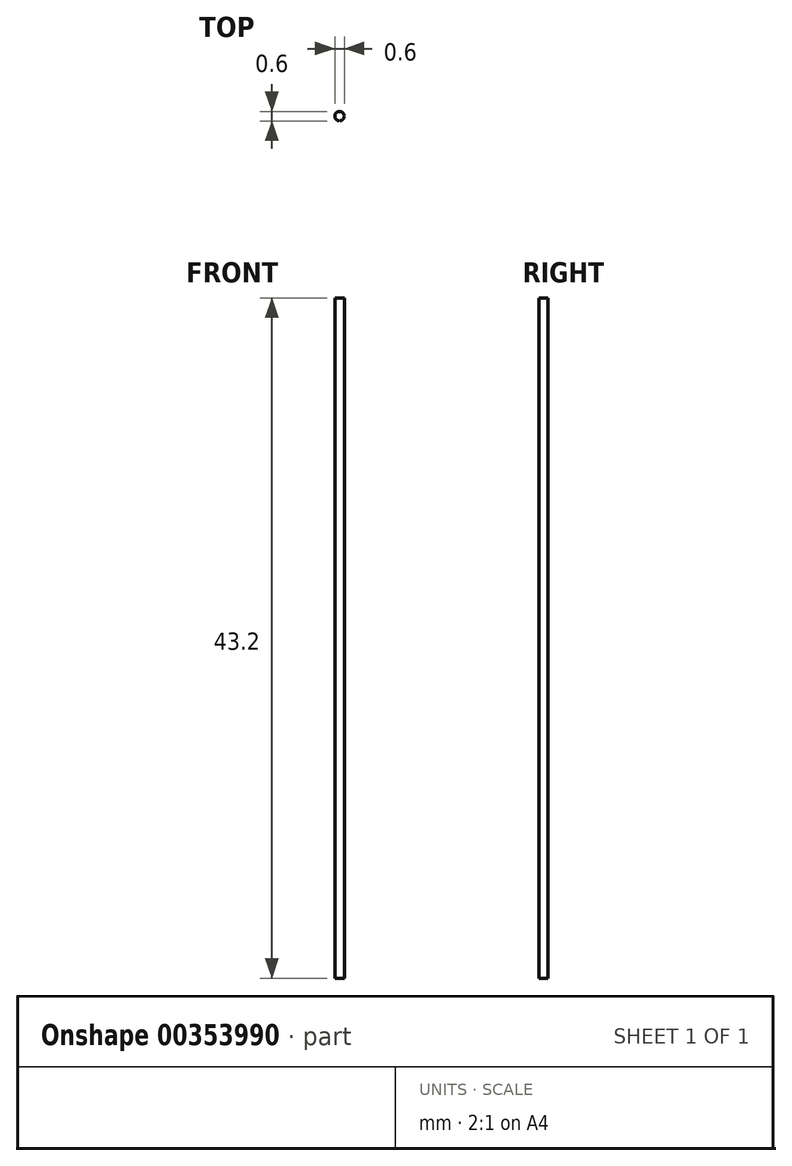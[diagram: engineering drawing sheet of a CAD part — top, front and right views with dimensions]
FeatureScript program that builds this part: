
annotation { "Feature Type Name" : "Feature", "Feature Type Description" : "" }
export const myFeature = defineFeature(function(context is Context, id is Id, definition is map)
    precondition{}
    {
        {
            var Q0;
            Q0=qCreatedBy(makeId("Top.planeOp"),FACE);
            var sketch = newSketch(context, id + "F0", { "sketchPlane" : qUnion([Q0])});
            skCircle(sketch, "E0", {"center": v(0, 0) * mm, "radius": 0.3 * mm});
            skSolve(sketch);
        }
        {
            var Q0;
            Q0 = qSketchRegion(id + "F0", true);
            extrude(context, id + "F1", {"entities" : qUnion([Q0]), "endBound" : BoundingType.SYMMETRIC, "depth" : 43.2 * mm});
        }
    });
